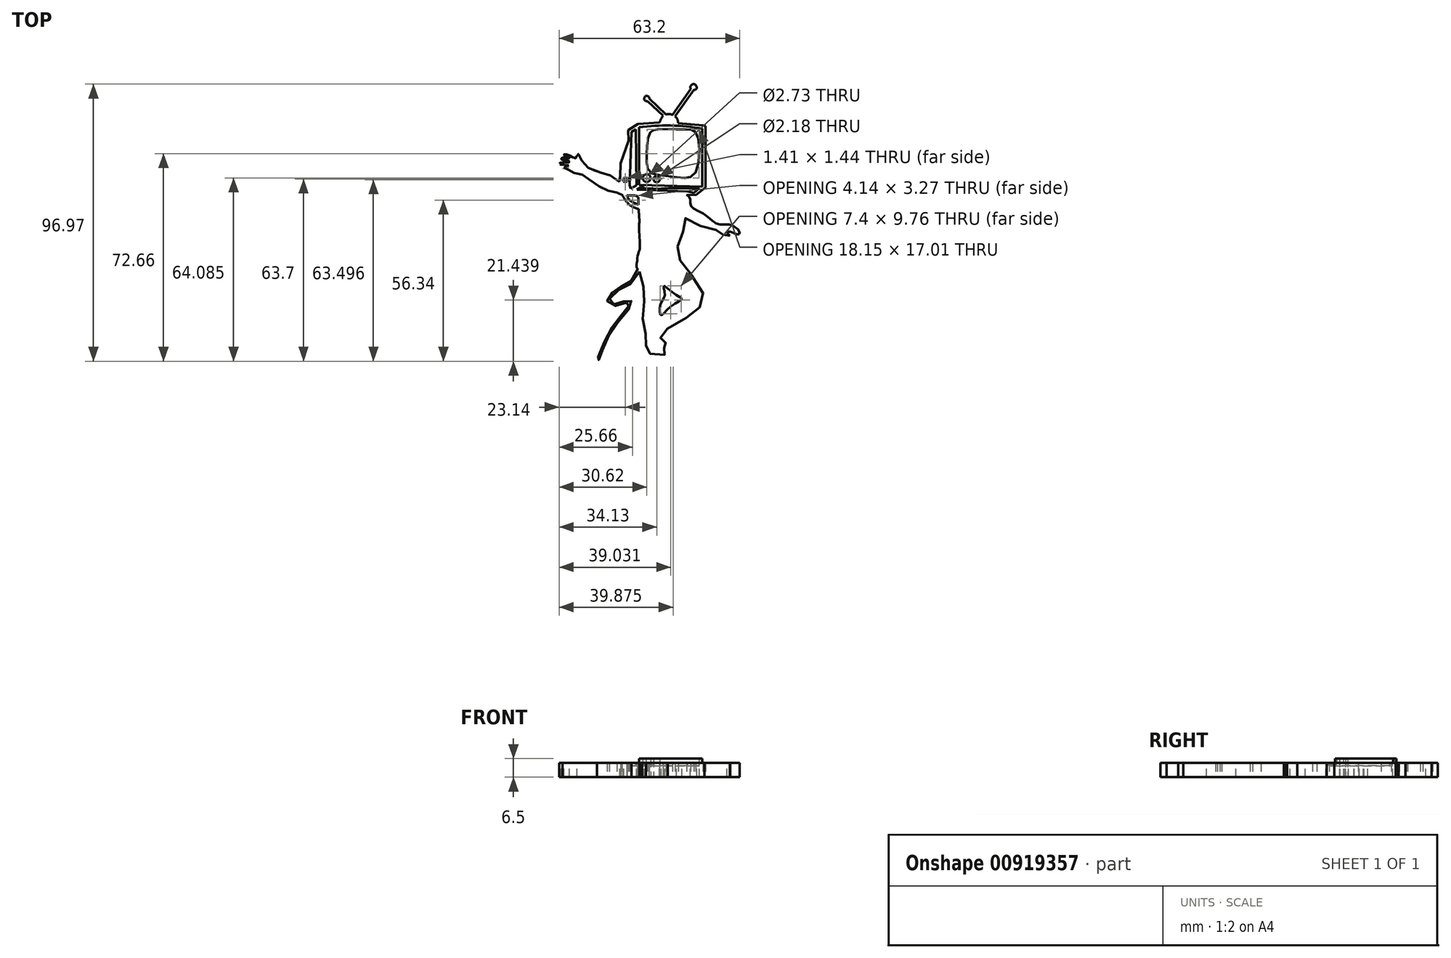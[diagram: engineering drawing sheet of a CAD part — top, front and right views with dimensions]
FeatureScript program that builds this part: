
annotation { "Feature Type Name" : "Feature", "Feature Type Description" : "" }
export const myFeature = defineFeature(function(context is Context, id is Id, definition is map)
    precondition{}
    {
        {
            var Q0;
            Q0=qCreatedBy(makeId("Top.planeOp"),FACE);
            var sketch = newSketch(context, id + "F0", { "sketchPlane" : qUnion([Q0])});
            skLineSegment(sketch, "E0", {"start": v(0, 0) * mm, "end": v(0, 130) * mm, "construction": true});
            skFitSpline(sketch, "E1", {"points": [v(-7.14, 40.36) * mm, v(-6.4, 43.97) * mm, v(-6.2, 46.41) * mm, v(-6.45, 51.93) * mm, v(-6.4, 54.52) * mm, v(-6.7, 59.55) * mm, v(-6.74, 61.07) * mm, v(-7.04, 62.87) * mm, v(-10.85, 63.22) * mm, v(-14.26, 64.25) * mm], "startDerivative": vector(-2.45, 46.5) * mm, "endDerivative": vector(-25.43, 12.1) * mm});
            skFitSpline(sketch, "E2", {"points": [v(-14.26, 64.25) * mm, v(-16.41, 64.78) * mm, v(-18.19, 65.1) * mm, v(-21.12, 66.94) * mm, v(-24.28, 69.07) * mm, v(-25.17, 69.62) * mm, v(-27.03, 70.92) * mm, v(-28.62, 71.03) * mm, v(-30.3, 71.7) * mm, v(-30.53, 72.09) * mm, v(-33.12, 72.61) * mm, v(-33.17, 73) * mm, v(-31, 73.07) * mm, v(-31.05, 73.64) * mm, v(-31.85, 73.92) * mm, v(-33.56, 73.99) * mm, v(-34.42, 74.3) * mm, v(-34.14, 74.71) * mm, v(-30.97, 74.79) * mm, v(-30.92, 75.16) * mm, v(-31.79, 75.45) * mm, v(-33.2, 75.62) * mm, v(-33.68, 76.05) * mm, v(-33.07, 76.51) * mm, v(-30.8, 76.25) * mm, v(-32.69, 77.27) * mm, v(-32.29, 77.7) * mm, v(-28.27, 76.19) * mm, v(-28.14, 76.97) * mm, v(-27.63, 77.77) * mm, v(-26.79, 75.87) * mm, v(-26.34, 75.26) * mm, v(-24.74, 73.3) * mm, v(-20.5, 71.32) * mm, v(-17.42, 70.59) * mm, v(-15.25, 69.4) * mm, v(-13.1, 68.2) * mm, v(-12.8, 69.97) * mm, v(-13.09, 70) * mm, v(-12.95, 74.45) * mm], "startDerivative": vector(-72.7, 19.87) * mm, "endDerivative": vector(6.97, 145.16) * mm});
            skLineSegment(sketch, "E3", {"start": v(-12.95, 74.45) * mm, "end": v(-10.16, 82.47) * mm});
            skLineSegment(sketch, "E4", {"start": v(-10.16, 82.47) * mm, "end": v(-10.24, 86.05) * mm});
            skLineSegment(sketch, "E5", {"start": v(-10.24, 86.05) * mm, "end": v(-6.85, 88.27) * mm});
            skLineSegment(sketch, "E6", {"start": v(-6.85, 88.27) * mm, "end": v(0.68, 88.75) * mm});
            skArc(sketch, "E7", {"start": v(1.92, 91.17) * mm, "mid": v(1.19, 90.02) * mm, "end": v(0.68, 88.75) * mm});
            skLineSegment(sketch, "E8", {"start": v(1.92, 91.17) * mm, "end": v(-3.36, 96.12) * mm});
            skFitSpline(sketch, "E9", {"points": [v(-3.36, 96.12) * mm, v(-4.53, 96.52) * mm, v(-4.63, 97.38) * mm, v(-4.04, 98.1) * mm, v(-3.08, 97.76) * mm, v(-2.97, 97.1) * mm], "startDerivative": vector(-6.18, 0.99) * mm, "endDerivative": vector(-0.42, -4.11) * mm});
            skLineSegment(sketch, "E10", {"start": v(-2.97, 97.1) * mm, "end": v(2.93, 91.58) * mm});
            skArc(sketch, "E11", {"start": v(5.24, 91.42) * mm, "mid": v(4.1, 91.7) * mm, "end": v(2.93, 91.58) * mm});
            skLineSegment(sketch, "E12", {"start": v(5.24, 91.42) * mm, "end": v(11.56, 100.49) * mm});
            skFitSpline(sketch, "E13", {"points": [v(11.56, 100.49) * mm, v(11.56, 101.58) * mm, v(12.55, 102.22) * mm, v(13.52, 101.58) * mm, v(13.54, 100.49) * mm, v(12.68, 100.16) * mm], "startDerivative": vector(-1.2, 5.7) * mm, "endDerivative": vector(-5.63, -0.79) * mm});
            skLineSegment(sketch, "E14", {"start": v(12.68, 100.16) * mm, "end": v(6.12, 90.98) * mm});
            skArc(sketch, "E15", {"start": v(7.19, 88.57) * mm, "mid": v(6.92, 89.9) * mm, "end": v(6.12, 90.98) * mm});
            skLineSegment(sketch, "E16", {"start": v(7.19, 88.57) * mm, "end": v(15.93, 87.76) * mm});
            skLineSegment(sketch, "E17", {"start": v(15.93, 87.76) * mm, "end": v(16.42, 87.59) * mm});
            skLineSegment(sketch, "E18", {"start": v(16.42, 87.59) * mm, "end": v(16.73, 87.47) * mm});
            skLineSegment(sketch, "E19", {"start": v(16.73, 87.47) * mm, "end": v(16.73, 66.1) * mm});
            skLineSegment(sketch, "E20", {"start": v(16.73, 66.1) * mm, "end": v(13.4, 63.39) * mm});
            skLineSegment(sketch, "E21", {"start": v(13.4, 63.39) * mm, "end": v(10.2, 63.45) * mm});
            skFitSpline(sketch, "E22", {"points": [v(10.2, 63.45) * mm, v(11.43, 61.9) * mm, v(11.65, 59.52) * mm, v(16.17, 56.79) * mm, v(21.06, 53.2) * mm, v(25.66, 52.9) * mm, v(28.75, 50.25) * mm, v(28.1, 49.53) * mm, v(26.6, 50.17) * mm, v(24.3, 50.53) * mm, v(25.3, 49.17) * mm], "startDerivative": vector(19.7, -16.41) * mm, "endDerivative": vector(23.14, -22.53) * mm});
            skFitSpline(sketch, "E23", {"points": [v(25.3, 49.17) * mm, v(25.3, 48.65) * mm, v(24.05, 48.6) * mm, v(22.74, 49.68) * mm, v(22.17, 49.85) * mm, v(20.85, 50.94) * mm, v(20.4, 51.16) * mm, v(17.65, 51.74) * mm, v(11.76, 53.9) * mm, v(9.64, 55.4) * mm, v(9.19, 55.85) * mm, v(8.84, 49.17) * mm, v(8.39, 48.42) * mm, v(6.61, 42.76) * mm, v(7.7, 41.03) * mm, v(8.1, 39.39) * mm, v(11.76, 35.73) * mm, v(16.1, 28.58) * mm, v(15.93, 25.2) * mm, v(12.68, 22.75) * mm, v(9.53, 20) * mm, v(3.3, 16.57) * mm, v(1.24, 15.03) * mm, v(1.01, 13.37) * mm, v(2.15, 13.2) * mm, v(3.13, 12.17) * mm, v(2.33, 11.48) * mm, v(1.3, 11.48) * mm, v(2.1, 10.05) * mm, v(3.3, 9.2) * mm, v(3.41, 7.88) * mm, v(0, 7.36) * mm, v(-2.36, 7.65) * mm, v(-3.5, 9.2) * mm, v(-3.74, 10.17) * mm, v(-4.08, 11.14) * mm, v(-3.9, 13.14) * mm, v(-4.3, 15.2) * mm, v(-4.88, 19.09) * mm, v(-5.45, 21.26) * mm, v(-4.6, 26.8) * mm, v(-4.25, 30.24) * mm, v(-5.9, 33.1) * mm, v(-6.37, 36.58) * mm, v(-7.34, 38.07) * mm, v(-7.14, 40.36) * mm], "startDerivative": vector(16.53, -55.96) * mm, "endDerivative": vector(24.03, 116.93) * mm});
            skFitSpline(sketch, "E24", {"points": [v(2.13, 31.57) * mm, v(2.54, 28.38) * mm, v(0.98, 25.18) * mm, v(1.18, 21.37) * mm, v(4.1, 24.1) * mm, v(8.46, 26.95) * mm, v(6.04, 28.75) * mm, v(2.13, 31.57) * mm]});
            skLineSegment(sketch, "E25", {"start": v(-11.67, 69.24) * mm, "end": v(-10.9, 69.24) * mm});
            skLineSegment(sketch, "E26", {"start": v(-10.9, 69.24) * mm, "end": v(-10.9, 67.94) * mm});
            skLineSegment(sketch, "E27", {"start": v(-10.9, 67.94) * mm, "end": v(-11.96, 67.99) * mm});
            skLineSegment(sketch, "E28", {"start": v(-11.96, 67.99) * mm, "end": v(-12, 69) * mm});
            skLineSegment(sketch, "E29", {"start": v(-12, 69) * mm, "end": v(-11.62, 69.29) * mm});
            skFitSpline(sketch, "E30", {"points": [v(-1.37, 86.05) * mm, v(-2.62, 85.2) * mm, v(-3.67, 80.67) * mm, v(-3.75, 74.12) * mm, v(-2.3, 71.2) * mm, v(4.09, 69.91) * mm, v(9.91, 69.35) * mm, v(13.39, 71.45) * mm, v(14.12, 83.5) * mm, v(12.46, 86.05) * mm, v(9.25, 86.33) * mm, v(0.25, 86.45) * mm, v(-1.37, 86.05) * mm]});
            skCircle(sketch, "E31", {"center": v(-3.82, 69.33) * mm, "radius": 1.36 * mm});
            skCircle(sketch, "E32", {"center": v(-0.31, 68.95) * mm, "radius": 1.09 * mm});
            skLineSegment(sketch, "E33", {"start": v(-9.07, 85.47) * mm, "end": v(-7.69, 86.38) * mm});
            skLineSegment(sketch, "E34", {"start": v(-7.69, 86.38) * mm, "end": v(-7.37, 66.93) * mm});
            skLineSegment(sketch, "E35", {"start": v(-7.37, 66.93) * mm, "end": v(-9.07, 65.47) * mm});
            skLineSegment(sketch, "E36", {"start": v(-9.07, 65.47) * mm, "end": v(-9.71, 66.69) * mm});
            skLineSegment(sketch, "E37", {"start": v(-9.71, 66.69) * mm, "end": v(-9.07, 85.47) * mm});
            skLineSegment(sketch, "E38", {"start": v(-6.46, 87.14) * mm, "end": v(-6.46, 66.91) * mm});
            skLineSegment(sketch, "E39", {"start": v(-6.46, 66.91) * mm, "end": v(15.56, 66.34) * mm});
            skLineSegment(sketch, "E40", {"start": v(15.56, 66.34) * mm, "end": v(15.56, 86.6) * mm});
            skArc(sketch, "E41", {"start": v(15.56, 86.6) * mm, "mid": v(4.57, 87.7) * mm, "end": v(-6.46, 87.14) * mm});
            skLineSegment(sketch, "E42", {"start": v(-7.23, 65.34) * mm, "end": v(-6.2, 66.05) * mm});
            skLineSegment(sketch, "E43", {"start": v(-6.2, 66.05) * mm, "end": v(14.6, 65.75) * mm});
            skLineSegment(sketch, "E44", {"start": v(14.6, 65.75) * mm, "end": v(12.66, 64.25) * mm});
            skLineSegment(sketch, "E45", {"start": v(12.66, 64.25) * mm, "end": v(10.56, 64.66) * mm});
            skLineSegment(sketch, "E46", {"start": v(10.56, 64.66) * mm, "end": v(-7.23, 64.97) * mm});
            skLineSegment(sketch, "E47", {"start": v(-7.23, 64.97) * mm, "end": v(-7.23, 65.34) * mm});
            skLineSegment(sketch, "E48", {"start": v(1.74, 88.93) * mm, "end": v(6.17, 88.61) * mm});
            skArc(sketch, "E49", {"start": v(6.17, 88.61) * mm, "mid": v(4.13, 90.64) * mm, "end": v(1.8, 88.96) * mm});
            skFitSpline(sketch, "E50", {"points": [v(-12.38, 63.49) * mm, v(-10.04, 60.15) * mm, v(-6.62, 58.5) * mm], "startDerivative": vector(4.02, -7.3) * mm, "endDerivative": vector(7.36, -2.62) * mm});
            skFitSpline(sketch, "E51", {"points": [v(-10.85, 63.22) * mm, v(-9.87, 61.69) * mm, v(-6.73, 59.96) * mm], "startDerivative": vector(1.97, -3.75) * mm, "endDerivative": vector(6.07, -2.83) * mm});
            skFitSpline(sketch, "E52", {"points": [v(-6.97, 37.48) * mm, v(-9, 33.63) * mm, v(-12.15, 31.6) * mm, v(-13.64, 30.88) * mm, v(-16.27, 28.91) * mm, v(-17.5, 26.94) * mm, v(-17.18, 25) * mm, v(-13.27, 24.85) * mm, v(-10.85, 25.77) * mm, v(-9.98, 26) * mm, v(-9.95, 25.08) * mm, v(-12.1, 22.04) * mm, v(-14.93, 18.6) * mm, v(-17.55, 14.44) * mm, v(-20.3, 7.93) * mm, v(-21.15, 5.35) * mm, v(-20.75, 5.3) * mm, v(-20.59, 6.03) * mm, v(-19.53, 8.54) * mm, v(-17.4, 13.43) * mm, v(-14.16, 18.57) * mm, v(-9.91, 23.7) * mm, v(-9.14, 25.6) * mm, v(-9.47, 26.61) * mm, v(-10.85, 26.57) * mm, v(-13.27, 25.48) * mm, v(-15.57, 25.2) * mm, v(-16.87, 26.2) * mm, v(-16.42, 27.75) * mm, v(-13.27, 30.37) * mm, v(-9.63, 32.11) * mm, v(-6.37, 36.58) * mm], "startDerivative": vector(-39.07, -105.55) * mm, "endDerivative": vector(66.83, 112.26) * mm});
            skSolve(sketch);
        }
        {
            var Q0;
            {var subQ9=sQuery(id+"F0.wireOp",EDGE,"E2");Q0=makeQuery(id+"F0.imprint","IMPRINT",FACE,{"disambiguationData":[TD([[makeQuery(id+"F0.imprint","IMPRINT",EDGE,{"derivedFrom":subQ9}),-1.0]])]});}
            var Q1;
            {var subQ0=sQuery(id+"F0.wireOp",EDGE,"E52");Q1=makeQuery(id+"F0.imprint","IMPRINT",FACE,{"disambiguationData":[TD([[makeQuery(id+"F0.imprint","IMPRINT",EDGE,{"derivedFrom":subQ0}),1.0]])]});}
            var Q2;
            {var subQ0=sQuery(id+"F0.wireOp",EDGE,"E50");Q2=makeQuery(id+"F0.imprint","IMPRINT",FACE,{"disambiguationData":[TD([[makeQuery(id+"F0.imprint","IMPRINT",EDGE,{"derivedFrom":subQ0}),1.0]])]});}
            extrude(context, id + "F1", {"entities" : qUnion([Q0, Q1, Q2]), "depth" : 2 * mm, "offsetDistance" : 25 * mm});
        }
        {
            var Q0;
            Q0=makeQuery(id+"F0.imprint","IMPRINT",FACE,{"disambiguationData":[TD([[makeQuery(id+"F0.imprint","IMPRINT",EDGE,{"derivedFrom":sQuery(id+"F0.wireOp",EDGE,"E33")}),-1.0]])]});
            var Q1;
            Q1=makeQuery(id+"F0.imprint","IMPRINT",FACE,{"disambiguationData":[TD([[makeQuery(id+"F0.imprint","IMPRINT",EDGE,{"derivedFrom":sQuery(id+"F0.wireOp",EDGE,"E42")}),-1.0]])]});
            extrude(context, id + "F2", {"entities" : qUnion([Q0, Q1]), "operationType" : NewBodyOperationType.ADD, "depth" : 2 * mm, "offsetDistance" : 25 * mm});
        }
        {
            var Q0;
            {var subQ0=sQuery(id+"F0.wireOp",EDGE,"E50");Q0=makeQuery(id+"F0.imprint","IMPRINT",FACE,{"disambiguationData":[TD([[makeQuery(id+"F0.imprint","IMPRINT",EDGE,{"derivedFrom":subQ0}),1.0]])]});}
            var Q1;
            Q1=makeQuery(id+"F2.opExtrude","CAP_FACE",FACE,{"disambiguationData":[OSD([sQuery(id+"F0.wireOp",EDGE,"E33"),sQuery(id+"F0.wireOp",EDGE,"E34"),sQuery(id+"F0.wireOp",EDGE,"E35"),sQuery(id+"F0.wireOp",EDGE,"E36"),sQuery(id+"F0.wireOp",EDGE,"E37")])],"isStart":false});
            var Q2;
            Q2=makeQuery(id+"F0.imprint","IMPRINT",FACE,{"disambiguationData":[TD([[makeQuery(id+"F0.imprint","IMPRINT",EDGE,{"derivedFrom":sQuery(id+"F0.wireOp",EDGE,"E30")}),-1.0]])]});
            var Q3;
            Q3=makeQuery(id+"F2.opExtrude","CAP_FACE",FACE,{"disambiguationData":[OSD([sQuery(id+"F0.wireOp",EDGE,"E42"),sQuery(id+"F0.wireOp",EDGE,"E43"),sQuery(id+"F0.wireOp",EDGE,"E44"),sQuery(id+"F0.wireOp",EDGE,"E45"),sQuery(id+"F0.wireOp",EDGE,"E46"),sQuery(id+"F0.wireOp",EDGE,"E47")])],"isStart":false});
            extrude(context, id + "F3", {"entities" : qUnion([Q0, Q1, Q2, Q3]), "operationType" : NewBodyOperationType.ADD, "depth" : 3 * mm, "offsetDistance" : 25 * mm});
        }
        {
            var Q0;
            Q0=makeQuery(id+"F3.opExtrude","CAP_FACE",FACE,{"disambiguationData":[OSD([sQuery(id+"F0.wireOp",EDGE,"E30"),sQuery(id+"F0.wireOp",EDGE,"E31"),sQuery(id+"F0.wireOp",EDGE,"E32"),sQuery(id+"F0.wireOp",EDGE,"E38"),sQuery(id+"F0.wireOp",EDGE,"E39"),sQuery(id+"F0.wireOp",EDGE,"E40"),sQuery(id+"F0.wireOp",EDGE,"E41")])],"isStart":false});
            extrude(context, id + "F4", {"entities" : qUnion([Q0]), "operationType" : NewBodyOperationType.ADD, "depth" : 3.5 * mm, "offsetDistance" : 25 * mm});
        }
        {
            var Q0;
            Q0=makeQuery(id+"F3.opExtrude","CAP_FACE",FACE,{"disambiguationData":[OSD([sQuery(id+"F0.wireOp",EDGE,"E1"),sQuery(id+"F0.wireOp",EDGE,"E2"),sQuery(id+"F0.wireOp",EDGE,"E3"),sQuery(id+"F0.wireOp",EDGE,"E4"),sQuery(id+"F0.wireOp",EDGE,"E5"),sQuery(id+"F0.wireOp",EDGE,"E6"),sQuery(id+"F0.wireOp",EDGE,"E7"),sQuery(id+"F0.wireOp",EDGE,"E8"),sQuery(id+"F0.wireOp",EDGE,"E9"),sQuery(id+"F0.wireOp",EDGE,"E10"),sQuery(id+"F0.wireOp",EDGE,"E11"),sQuery(id+"F0.wireOp",EDGE,"E12"),sQuery(id+"F0.wireOp",EDGE,"E13"),sQuery(id+"F0.wireOp",EDGE,"E14"),sQuery(id+"F0.wireOp",EDGE,"E15"),sQuery(id+"F0.wireOp",EDGE,"E16"),sQuery(id+"F0.wireOp",EDGE,"E17"),sQuery(id+"F0.wireOp",EDGE,"E18"),sQuery(id+"F0.wireOp",EDGE,"E19"),sQuery(id+"F0.wireOp",EDGE,"E20"),sQuery(id+"F0.wireOp",EDGE,"E21"),sQuery(id+"F0.wireOp",EDGE,"E22"),sQuery(id+"F0.wireOp",EDGE,"E23"),sQuery(id+"F0.wireOp",EDGE,"E24"),sQuery(id+"F0.wireOp",EDGE,"E33"),sQuery(id+"F0.wireOp",EDGE,"E34"),sQuery(id+"F0.wireOp",EDGE,"E35"),sQuery(id+"F0.wireOp",EDGE,"E36"),sQuery(id+"F0.wireOp",EDGE,"E37"),sQuery(id+"F0.wireOp",EDGE,"E38"),sQuery(id+"F0.wireOp",EDGE,"E39"),sQuery(id+"F0.wireOp",EDGE,"E40"),sQuery(id+"F0.wireOp",EDGE,"E41"),sQuery(id+"F0.wireOp",EDGE,"E42"),sQuery(id+"F0.wireOp",EDGE,"E43"),sQuery(id+"F0.wireOp",EDGE,"E44"),sQuery(id+"F0.wireOp",EDGE,"E45"),sQuery(id+"F0.wireOp",EDGE,"E46"),sQuery(id+"F0.wireOp",EDGE,"E47"),sQuery(id+"F0.wireOp",EDGE,"E52")])],"isStart":false});
            var sketch = newSketch(context, id + "F5", { "sketchPlane" : qUnion([Q0])});
            skLineSegment(sketch, "E53", {"start": v(-7.65, 86.4) * mm, "end": v(-9.11, 85.48) * mm});
            skLineSegment(sketch, "E54", {"start": v(-9.11, 85.48) * mm, "end": v(-9.77, 66.86) * mm});
            skLineSegment(sketch, "E55", {"start": v(-9.77, 66.86) * mm, "end": v(-9.43, 65.64) * mm});
            skLineSegment(sketch, "E56", {"start": v(-9.43, 65.64) * mm, "end": v(-7.38, 66.78) * mm});
            skLineSegment(sketch, "E57", {"start": v(-7.38, 66.78) * mm, "end": v(-7.65, 86.4) * mm});
            skLineSegment(sketch, "E58", {"start": v(-6, 66.09) * mm, "end": v(-7.27, 65.23) * mm});
            skLineSegment(sketch, "E59", {"start": v(-7.27, 65.23) * mm, "end": v(10.52, 64.66) * mm});
            skLineSegment(sketch, "E60", {"start": v(10.52, 64.66) * mm, "end": v(12.66, 64.2) * mm});
            skLineSegment(sketch, "E61", {"start": v(12.66, 64.2) * mm, "end": v(14.55, 65.77) * mm});
            skLineSegment(sketch, "E62", {"start": v(14.55, 65.77) * mm, "end": v(3.77, 65.77) * mm});
            skLineSegment(sketch, "E63", {"start": v(3.77, 65.77) * mm, "end": v(-1.26, 65.49) * mm});
            skLineSegment(sketch, "E64", {"start": v(-1.26, 65.49) * mm, "end": v(-1.86, 65.74) * mm});
            skLineSegment(sketch, "E65", {"start": v(-1.86, 65.74) * mm, "end": v(-4.27, 65.71) * mm});
            skLineSegment(sketch, "E66", {"start": v(-4.27, 65.71) * mm, "end": v(-4.78, 66.03) * mm});
            skLineSegment(sketch, "E67", {"start": v(-4.78, 66.03) * mm, "end": v(-6, 66.09) * mm});
            skSolve(sketch);
        }
        {
            var Q0;
            Q0 = qSketchRegion(id + "F5", true);
            extrude(context, id + "F6", {"entities" : qUnion([Q0]), "operationType" : NewBodyOperationType.REMOVE, "oppositeDirection" : true, "depth" : 1 * mm, "offsetDistance" : 25 * mm});
        }
        {
            var Q0;
            Q0=makeQuery(id+"F3.opExtrude","CAP_FACE",FACE,{"disambiguationData":[OSD([sQuery(id+"F0.wireOp",EDGE,"E1"),sQuery(id+"F0.wireOp",EDGE,"E2"),sQuery(id+"F0.wireOp",EDGE,"E3"),sQuery(id+"F0.wireOp",EDGE,"E4"),sQuery(id+"F0.wireOp",EDGE,"E5"),sQuery(id+"F0.wireOp",EDGE,"E6"),sQuery(id+"F0.wireOp",EDGE,"E7"),sQuery(id+"F0.wireOp",EDGE,"E8"),sQuery(id+"F0.wireOp",EDGE,"E9"),sQuery(id+"F0.wireOp",EDGE,"E10"),sQuery(id+"F0.wireOp",EDGE,"E11"),sQuery(id+"F0.wireOp",EDGE,"E12"),sQuery(id+"F0.wireOp",EDGE,"E13"),sQuery(id+"F0.wireOp",EDGE,"E14"),sQuery(id+"F0.wireOp",EDGE,"E15"),sQuery(id+"F0.wireOp",EDGE,"E16"),sQuery(id+"F0.wireOp",EDGE,"E17"),sQuery(id+"F0.wireOp",EDGE,"E18"),sQuery(id+"F0.wireOp",EDGE,"E19"),sQuery(id+"F0.wireOp",EDGE,"E20"),sQuery(id+"F0.wireOp",EDGE,"E21"),sQuery(id+"F0.wireOp",EDGE,"E22"),sQuery(id+"F0.wireOp",EDGE,"E23"),sQuery(id+"F0.wireOp",EDGE,"E24"),sQuery(id+"F0.wireOp",EDGE,"E33"),sQuery(id+"F0.wireOp",EDGE,"E34"),sQuery(id+"F0.wireOp",EDGE,"E35"),sQuery(id+"F0.wireOp",EDGE,"E36"),sQuery(id+"F0.wireOp",EDGE,"E37"),sQuery(id+"F0.wireOp",EDGE,"E38"),sQuery(id+"F0.wireOp",EDGE,"E39"),sQuery(id+"F0.wireOp",EDGE,"E40"),sQuery(id+"F0.wireOp",EDGE,"E41"),sQuery(id+"F0.wireOp",EDGE,"E42"),sQuery(id+"F0.wireOp",EDGE,"E43"),sQuery(id+"F0.wireOp",EDGE,"E44"),sQuery(id+"F0.wireOp",EDGE,"E45"),sQuery(id+"F0.wireOp",EDGE,"E46"),sQuery(id+"F0.wireOp",EDGE,"E47"),sQuery(id+"F0.wireOp",EDGE,"E50"),sQuery(id+"F0.wireOp",EDGE,"E51"),sQuery(id+"F0.wireOp",EDGE,"E52")])],"isStart":false});
            var sketch = newSketch(context, id + "F7", { "sketchPlane" : qUnion([Q0])});
            skLineSegment(sketch, "E68", {"start": v(-11.77, 69.47) * mm, "end": v(-12, 68.07) * mm});
            skLineSegment(sketch, "E69", {"start": v(-12, 68.07) * mm, "end": v(-10.63, 68.03) * mm});
            skLineSegment(sketch, "E70", {"start": v(-10.63, 68.03) * mm, "end": v(-10.6, 69.37) * mm});
            skLineSegment(sketch, "E71", {"start": v(-10.6, 69.37) * mm, "end": v(-11.77, 69.47) * mm});
            skSolve(sketch);
        }
        {
            var Q0;
            Q0=makeQuery(id+"F7.imprint","IMPRINT",FACE,{"disambiguationData":[TD([[makeQuery(id+"F7.imprint","IMPRINT",EDGE,{"derivedFrom":sQuery(id+"F7.wireOp",EDGE,"E68")}),1.0]])]});
            extrude(context, id + "F8", {"entities" : qUnion([Q0]), "operationType" : NewBodyOperationType.REMOVE, "oppositeDirection" : true, "depth" : 10 * mm, "offsetDistance" : 25 * mm});
        }
    });
